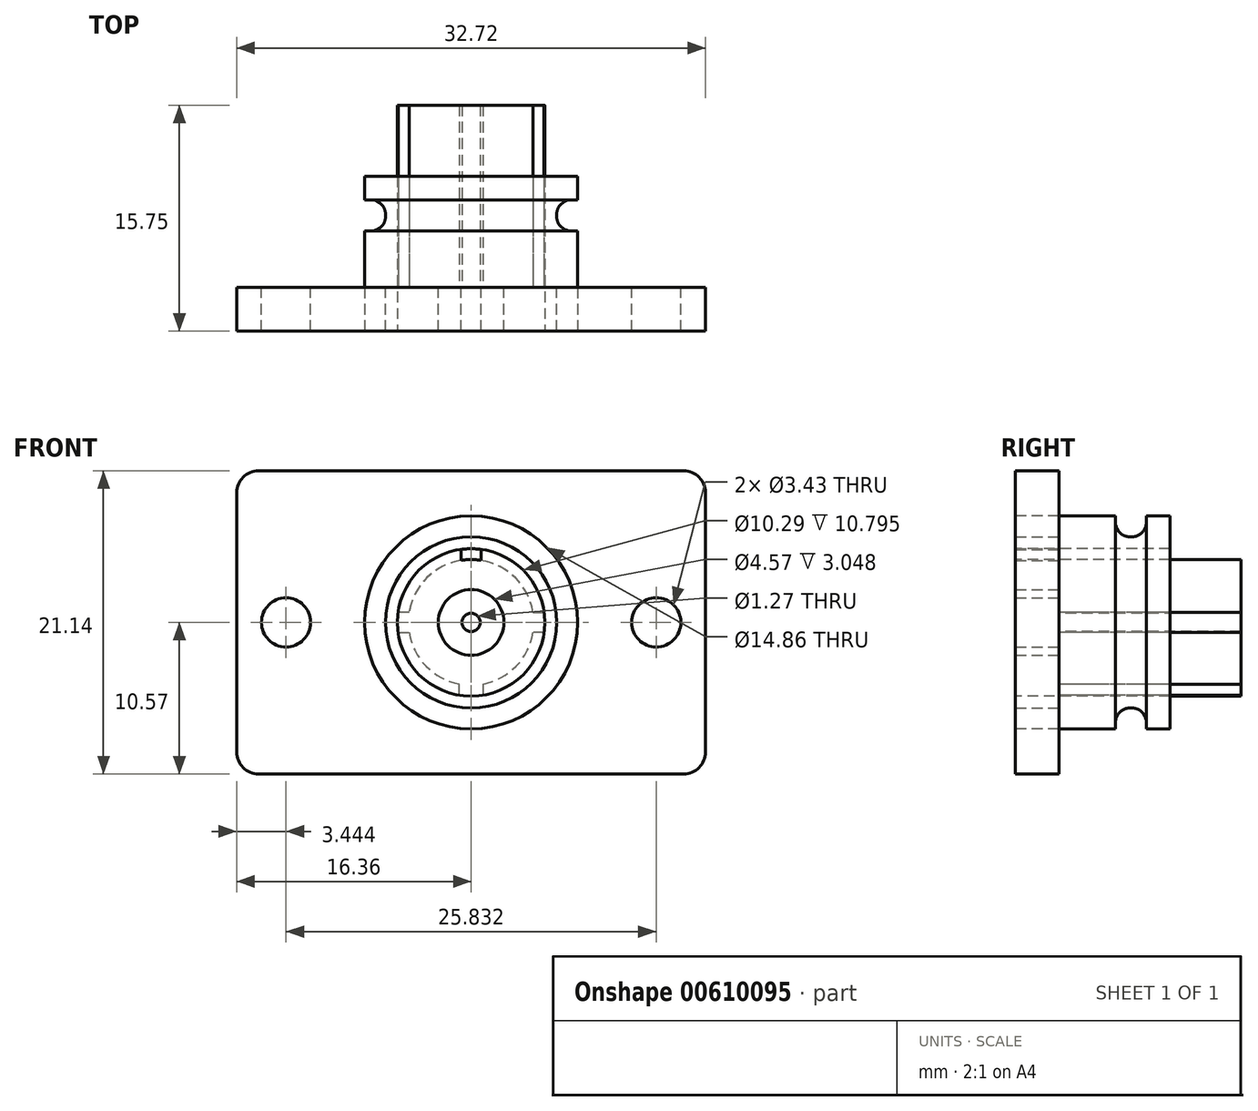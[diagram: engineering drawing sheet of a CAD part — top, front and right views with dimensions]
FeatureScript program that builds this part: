
annotation { "Feature Type Name" : "Feature", "Feature Type Description" : "" }
export const myFeature = defineFeature(function(context is Context, id is Id, definition is map)
    precondition{}
    {
        {
            var Q0;
            Q0=qCreatedBy(makeId("Front.planeOp"),FACE);
            var sketch = newSketch(context, id + "F0", { "sketchPlane" : qUnion([Q0])});
            skLineSegment(sketch, "E0.bottom", {"start": v(14.83, 10.57) * mm, "end": v(-14.83, 10.57) * mm});
            skLineSegment(sketch, "E0.top", {"start": v(14.83, -10.57) * mm, "end": v(-14.83, -10.57) * mm});
            skLineSegment(sketch, "E0.left", {"start": v(16.36, 9.04) * mm, "end": v(16.36, -9.04) * mm});
            skLineSegment(sketch, "E0.right", {"start": v(-16.36, 9.04) * mm, "end": v(-16.36, -9.04) * mm});
            skPoint(sketch, "E0.middle", {"position": v(0, 0) * mm});
            skCircle(sketch, "E1", {"center": v(12.92, 0) * mm, "radius": 1.71 * mm});
            skCircle(sketch, "E2", {"center": v(-12.92, 0) * mm, "radius": 1.71 * mm});
            skCircle(sketch, "E3", {"center": v(0, 0) * mm, "radius": 2.03 * mm});
            skCircle(sketch, "E4", {"center": v(0, 0) * mm, "radius": 2.29 * mm});
            skCircle(sketch, "E5", {"center": v(0, 0) * mm, "radius": 4.38 * mm});
            skLineSegment(sketch, "E6", {"start": v(-4.33, 0.7) * mm, "end": v(-5.09, 0.7) * mm});
            skLineSegment(sketch, "E7", {"start": v(-5.09, -0.7) * mm, "end": v(-4.33, -0.7) * mm});
            skLineSegment(sketch, "E8", {"start": v(4.33, 0.7) * mm, "end": v(5.09, 0.7) * mm});
            skLineSegment(sketch, "E9", {"start": v(5.09, -0.7) * mm, "end": v(4.33, -0.7) * mm});
            skLineSegment(sketch, "E10", {"start": v(0.7, 4.33) * mm, "end": v(0.7, 5.09) * mm});
            skLineSegment(sketch, "E11", {"start": v(-0.7, 5.09) * mm, "end": v(-0.7, 4.33) * mm});
            skArc(sketch, "E12", {"start": v(-5.09, 0.7) * mm, "mid": v(3.63, -3.63) * mm, "end": v(-0.7, 5.09) * mm});
            skLineSegment(sketch, "E13", {"start": v(-0.7, 5.09) * mm, "end": v(-0.7, 5.09) * mm});
            skLineSegment(sketch, "E14.MirrorCS", {"start": v(0.7, 5.09) * mm, "end": v(0.7, 4.33) * mm});
            skLineSegment(sketch, "E15.MirrorCS", {"start": v(-0.7, 4.33) * mm, "end": v(-0.7, 5.09) * mm});
            skArc(sketch, "E16", {"start": v(-0.7, 5.09) * mm, "mid": v(-3.63, 3.63) * mm, "end": v(-5.09, 0.7) * mm});
            skLineSegment(sketch, "E17", {"start": v(0.82, -4.3) * mm, "end": v(0.82, -5.07) * mm});
            skLineSegment(sketch, "E18", {"start": v(-0.82, -5.07) * mm, "end": v(-0.82, -4.3) * mm});
            skCircle(sketch, "E19", {"center": v(0, 0) * mm, "radius": 7.43 * mm});
            skCircle(sketch, "E20", {"center": v(0, 0) * mm, "radius": 5.97 * mm});
            skPoint(sketch, "E21.visualSharp", {"position": v(-16.36, 10.57) * mm});
            skArc(sketch, "E21.filletArc", {"start": v(-14.83, 10.57) * mm, "mid": v(-15.91, 10.12) * mm, "end": v(-16.36, 9.04) * mm});
            skPoint(sketch, "E22.visualSharp", {"position": v(-16.36, -10.57) * mm});
            skArc(sketch, "E22.filletArc", {"start": v(-16.36, -9.04) * mm, "mid": v(-15.91, -10.12) * mm, "end": v(-14.83, -10.57) * mm});
            skPoint(sketch, "E23.visualSharp", {"position": v(16.36, -10.57) * mm});
            skArc(sketch, "E23.filletArc", {"start": v(14.83, -10.57) * mm, "mid": v(15.91, -10.12) * mm, "end": v(16.36, -9.04) * mm});
            skPoint(sketch, "E24.visualSharp", {"position": v(16.36, 10.57) * mm});
            skArc(sketch, "E24.filletArc", {"start": v(16.36, 9.04) * mm, "mid": v(15.91, 10.12) * mm, "end": v(14.83, 10.57) * mm});
            skPoint(sketch, "E25.endSnap0", {"position": v(-16.36, 0) * mm});
            skCircle(sketch, "E26", {"center": v(0, 0) * mm, "radius": 0.64 * mm});
            skSolve(sketch);
        }
        {
            var Q0;
            Q0 = qSketchRegion(id + "F0", true);
            extrude(context, id + "F1", {"entities" : qUnion([Q0]), "depth" : 3.05 * mm, "offsetDistance" : 25.4 * mm});
        }
        {
            var Q0;
            {var subQ0=sQuery(id+"F0.wireOp",EDGE,"E8");Q0=makeQuery(id+"F0.imprint","IMPRINT",FACE,{"disambiguationData":[TD([[makeQuery(id+"F0.imprint","IMPRINT",EDGE,{"derivedFrom":subQ0}),-1.0]])]});}
            var Q1;
            Q1=makeQuery(id+"F0.imprint","IMPRINT",FACE,{"disambiguationData":[TD([[makeQuery(id+"F0.imprint","IMPRINT",EDGE,{"derivedFrom":sQuery(id+"F0.wireOp",EDGE,"E4")}),-1.0]])]});
            var Q2;
            {var subQ0=sQuery(id+"F0.wireOp",EDGE,"E17");Q2=makeQuery(id+"F0.imprint","IMPRINT",FACE,{"disambiguationData":[TD([[makeQuery(id+"F0.imprint","IMPRINT",EDGE,{"derivedFrom":subQ0}),-1.0]])]});}
            var Q3;
            {var subQ0=sQuery(id+"F0.wireOp",EDGE,"E6");Q3=makeQuery(id+"F0.imprint","IMPRINT",FACE,{"disambiguationData":[TD([[makeQuery(id+"F0.imprint","IMPRINT",EDGE,{"derivedFrom":subQ0}),1.0]])]});}
            var Q4;
            Q4=makeQuery(id+"F0.imprint","IMPRINT",FACE,{"disambiguationData":[TD([[makeQuery(id+"F0.imprint","IMPRINT",EDGE,{"derivedFrom":sQuery(id+"F0.wireOp",EDGE,"8aa54b31-4197-416b-9f73-8f9571a17bba2.MirrorCS")}),-1.0]])]});
            var Q5;
            {var subQ0=sQuery(id+"F0.wireOp",EDGE,"E15.MirrorCS");Q5=makeQuery(id+"F0.imprint","IMPRINT",FACE,{"disambiguationData":[TD([[makeQuery(id+"F0.imprint","IMPRINT",EDGE,{"derivedFrom":subQ0}),-1.0]])]});}
            var Q6;
            Q6=makeQuery(id+"F0.imprint","IMPRINT",FACE,{"disambiguationData":[TD([[makeQuery(id+"F0.imprint","IMPRINT",EDGE,{"derivedFrom":sQuery(id+"F0.wireOp",EDGE,"E3")}),-1.0]])]});
            extrude(context, id + "F2", {"entities" : qUnion([Q0, Q1, Q2, Q3, Q4, Q5, Q6]), "depth" : -12.7 * mm, "offsetDistance" : 25.4 * mm});
        }
        {
            var Q0;
            {var subQ0=sQuery(id+"F0.wireOp",EDGE,"ZeHlMGJi-U5nD-rJSf-8bKy-MKMc3yEPTVGU");Q0=makeQuery(id+"F0.imprint","IMPRINT",FACE,{"disambiguationData":[TD([[makeQuery(id+"F0.imprint","IMPRINT",EDGE,{"derivedFrom":subQ0}),1.0]])]});}
            var Q1;
            {var subQ0=sQuery(id+"F0.wireOp",EDGE,"E8");Q1=makeQuery(id+"F0.imprint","IMPRINT",FACE,{"disambiguationData":[TD([[makeQuery(id+"F0.imprint","IMPRINT",EDGE,{"derivedFrom":subQ0}),-1.0]])]});}
            var Q2;
            {var subQ8=sQuery(id+"F0.wireOp",EDGE,"E16");Q2=makeQuery(id+"F0.imprint","IMPRINT",FACE,{"disambiguationData":[TD([[makeQuery(id+"F0.imprint","IMPRINT",EDGE,{"derivedFrom":subQ8}),-1.0]])]});}
            var Q3;
            {var subQ0=sQuery(id+"F0.wireOp",EDGE,"E9");Q3=makeQuery(id+"F0.imprint","IMPRINT",FACE,{"disambiguationData":[TD([[makeQuery(id+"F0.imprint","IMPRINT",EDGE,{"derivedFrom":subQ0}),1.0]])]});}
            var Q4;
            Q4=makeQuery(id+"F0.imprint","IMPRINT",FACE,{"disambiguationData":[TD([[makeQuery(id+"F0.imprint","IMPRINT",EDGE,{"derivedFrom":sQuery(id+"F0.wireOp",EDGE,"E4")}),-1.0]])]});
            var Q5;
            {var subQ0=sQuery(id+"F0.wireOp",EDGE,"E8");Q5=makeQuery(id+"F0.imprint","IMPRINT",FACE,{"disambiguationData":[TD([[makeQuery(id+"F0.imprint","IMPRINT",EDGE,{"derivedFrom":subQ0}),1.0]])]});}
            var Q6;
            {var subQ0=sQuery(id+"F0.wireOp",EDGE,"E17");Q6=makeQuery(id+"F0.imprint","IMPRINT",FACE,{"disambiguationData":[TD([[makeQuery(id+"F0.imprint","IMPRINT",EDGE,{"derivedFrom":subQ0}),-1.0]])]});}
            var Q7;
            {var subQ0=sQuery(id+"F0.wireOp",EDGE,"E7");Q7=makeQuery(id+"F0.imprint","IMPRINT",FACE,{"disambiguationData":[TD([[makeQuery(id+"F0.imprint","IMPRINT",EDGE,{"derivedFrom":subQ0}),-1.0]])]});}
            var Q8;
            {var subQ0=sQuery(id+"F0.wireOp",EDGE,"E6");Q8=makeQuery(id+"F0.imprint","IMPRINT",FACE,{"disambiguationData":[TD([[makeQuery(id+"F0.imprint","IMPRINT",EDGE,{"derivedFrom":subQ0}),1.0]])]});}
            var Q9;
            {var subQ0=sQuery(id+"F0.wireOp",EDGE,"E6");Q9=makeQuery(id+"F0.imprint","IMPRINT",FACE,{"disambiguationData":[TD([[makeQuery(id+"F0.imprint","IMPRINT",EDGE,{"derivedFrom":subQ0}),-1.0]])]});}
            var Q10;
            Q10=makeQuery(id+"F0.imprint","IMPRINT",FACE,{"disambiguationData":[TD([[makeQuery(id+"F0.imprint","IMPRINT",EDGE,{"derivedFrom":sQuery(id+"F0.wireOp",EDGE,"8aa54b31-4197-416b-9f73-8f9571a17bba2.MirrorCS")}),-1.0]])]});
            var Q11;
            {var subQ0=sQuery(id+"F0.wireOp",EDGE,"8aa54b31-4197-416b-9f73-8f9571a17bba2.MirrorCS");Q11=makeQuery(id+"F0.imprint","IMPRINT",FACE,{"disambiguationData":[TD([[makeQuery(id+"F0.imprint","IMPRINT",EDGE,{"derivedFrom":subQ0}),1.0]])]});}
            var Q12;
            {var subQ0=sQuery(id+"F0.wireOp",EDGE,"5Tk1WabR-ANaY-RywQ-UzY8-5ZMrk3N4MROS");Q12=makeQuery(id+"F0.imprint","IMPRINT",FACE,{"disambiguationData":[TD([[makeQuery(id+"F0.imprint","IMPRINT",EDGE,{"derivedFrom":subQ0}),-1.0]])]});}
            var Q13;
            {var subQ0=sQuery(id+"F0.wireOp",EDGE,"8KnzkotE-2pe1-5BcI-FaJd-2mQ7kcLGwGro");Q13=makeQuery(id+"F0.imprint","IMPRINT",FACE,{"disambiguationData":[TD([[makeQuery(id+"F0.imprint","IMPRINT",EDGE,{"derivedFrom":subQ0}),1.0]])]});}
            var Q14;
            {var subQ0=sQuery(id+"F0.wireOp",EDGE,"E15.MirrorCS");Q14=makeQuery(id+"F0.imprint","IMPRINT",FACE,{"disambiguationData":[TD([[makeQuery(id+"F0.imprint","IMPRINT",EDGE,{"derivedFrom":subQ0}),-1.0]])]});}
            extrude(context, id + "F3", {"entities" : qUnion([Q0, Q1, Q2, Q3, Q4, Q5, Q6, Q7, Q8, Q9, Q10, Q11, Q12, Q13, Q14]), "depth" : 3.05 * mm, "offsetDistance" : 25.4 * mm});
        }
        {
            var Q0;
            Q0=qCreatedBy(makeId("Right.planeOp"),FACE);
            var sketch = newSketch(context, id + "F4", { "sketchPlane" : qUnion([Q0])});
            skLineSegment(sketch, "E27", {"start": v(0, 0) * mm, "end": v(19.56, 0) * mm, "construction": true});
            skLineSegment(sketch, "E28", {"start": v(-3.05, 5.14) * mm, "end": v(7.75, 5.14) * mm});
            skLineSegment(sketch, "E29", {"start": v(7.75, 5.14) * mm, "end": v(7.75, 7.43) * mm});
            skLineSegment(sketch, "E30", {"start": v(-3.05, 5.14) * mm, "end": v(-3.05, 7.43) * mm});
            skLineSegment(sketch, "E31", {"start": v(7.75, 7.43) * mm, "end": v(6.1, 7.43) * mm});
            skLineSegment(sketch, "E32", {"start": v(6.1, 7.43) * mm, "end": v(6.1, 5.97) * mm});
            skLineSegment(sketch, "E33", {"start": v(6.1, 5.97) * mm, "end": v(3.94, 5.97) * mm});
            skLineSegment(sketch, "E34", {"start": v(3.94, 5.97) * mm, "end": v(3.94, 7.43) * mm});
            skLineSegment(sketch, "E35", {"start": v(3.94, 7.43) * mm, "end": v(-3.05, 7.43) * mm});
            skLineSegment(sketch, "E36", {"start": v(-4.57, -2.29) * mm, "end": v(-10.67, -2.29) * mm});
            skPoint(sketch, "E37.visualSharp", {"position": v(-3.05, -2.29) * mm});
            skArc(sketch, "E37.filletArc", {"start": v(-3.05, -3.81) * mm, "mid": v(-3.5, -2.73) * mm, "end": v(-4.57, -2.29) * mm});
            skPoint(sketch, "E38.visualSharp", {"position": v(-3.05, 2.29) * mm});
            skLineSegment(sketch, "E39", {"start": v(-3.05, 0) * mm, "end": v(-10.67, 0) * mm});
            skLineSegment(sketch, "E40", {"start": v(-3.05, 0) * mm, "end": v(-3.05, 0.63) * mm});
            skLineSegment(sketch, "E41", {"start": v(-3.05, 0.63) * mm, "end": v(-10.67, 0.63) * mm});
            skLineSegment(sketch, "E42", {"start": v(-10.67, 0.63) * mm, "end": v(-10.67, -0.64) * mm});
            skLineSegment(sketch, "E43", {"start": v(-10.67, -0.64) * mm, "end": v(-3.05, -0.64) * mm});
            skLineSegment(sketch, "E44", {"start": v(-3.05, -0.64) * mm, "end": v(-3.05, 0) * mm});
            skLineSegment(sketch, "E45", {"start": v(-3.05, -3.81) * mm, "end": v(-3.05, -0.64) * mm});
            skLineSegment(sketch, "E46", {"start": v(-10.67, -2.29) * mm, "end": v(-10.67, -0.64) * mm});
            skLineSegment(sketch, "E47", {"start": v(-3.05, -2.29) * mm, "end": v(0, -2.29) * mm});
            skLineSegment(sketch, "E48", {"start": v(-3.05, 2.29) * mm, "end": v(0, 2.29) * mm});
            skLineSegment(sketch, "E49", {"start": v(0, 0) * mm, "end": v(-3.05, 0) * mm});
            skLineSegment(sketch, "E50", {"start": v(-3.05, 0.63) * mm, "end": v(0, 0.63) * mm});
            skLineSegment(sketch, "E51", {"start": v(-3.05, -0.64) * mm, "end": v(0, -0.64) * mm});
            skLineSegment(sketch, "E52", {"start": v(-3.05, 2.29) * mm, "end": v(-3.05, 0.63) * mm});
            skLineSegment(sketch, "E53", {"start": v(0, 2.29) * mm, "end": v(0, 0.63) * mm});
            skSolve(sketch);
        }
        {
            var Q0;
            Q0=makeQuery(id+"F4.imprint","IMPRINT",FACE,{"disambiguationData":[TD([[makeQuery(id+"F4.imprint","IMPRINT",EDGE,{"derivedFrom":sQuery(id+"F4.wireOp",EDGE,"E28")}),1.0]])]});
            var Q1;
            Q1=sQuery(id+"F4.wireOp",EDGE,"E27");
            revolve(context, id + "F5", {"entities" : qUnion([Q0]), "axis" : qUnion([Q1]), "revolveType" : RevolveType.FULL});
        }
        {
            var Q0;
            Q0=makeQuery(id+"F5.opRevolve","SWEPT_EDGE",EDGE,{"disambiguationData":[OSD([sQuery(id+"F4.wireOp",EDGE,"E32"),sQuery(id+"F4.wireOp",EDGE,"E33")])]});
            var Q1;
            Q1=makeQuery(id+"F5.opRevolve","SWEPT_EDGE",EDGE,{"disambiguationData":[OSD([sQuery(id+"F4.wireOp",EDGE,"E33"),sQuery(id+"F4.wireOp",EDGE,"E34")])]});
            fillet(context, id + "F6", {"entities" : qUnion([Q0, Q1]), "radius" : 1.02 * mm, "tangentPropagation" : true, "allowEdgeOverflow" : false});
        }
        {
            var Q0;
            Q0 = qSketchRegion(id + "F4", true);
            var Q1;
            Q1=sQuery(id+"F4.wireOp",EDGE,"E43");
            var Q2;
            Q2=sQuery(id+"F4.wireOp",EDGE,"E45");
            var Q3;
            Q3=sQuery(id+"F4.wireOp",EDGE,"E37.filletArc");
            var Q4;
            Q4=sQuery(id+"F4.wireOp",EDGE,"E36");
            var Q5;
            Q5=sQuery(id+"F4.wireOp",EDGE,"E46");
            var Q6;
            Q6=sQuery(id+"F4.wireOp",EDGE,"E39");
            revolve(context, id + "F7", {"bodyType" : ToolBodyType.SURFACE, "entities" : qUnion([Q0]), "surfaceEntities" : qUnion([Q1, Q2, Q3, Q4, Q5]), "axis" : qUnion([Q6]), "revolveType" : RevolveType.FULL});
        }
        {
            var Q0;
            Q0 = qSketchRegion(id + "F4", true);
            var Q1;
            Q1=sQuery(id+"F4.wireOp",EDGE,"E48");
            var Q2;
            Q2=sQuery(id+"F4.wireOp",EDGE,"E50");
            var Q3;
            Q3=sQuery(id+"F4.wireOp",EDGE,"E52");
            var Q4;
            Q4=sQuery(id+"F4.wireOp",EDGE,"E53");
            var Q5;
            Q5=sQuery(id+"F4.wireOp",EDGE,"E49");
            revolve(context, id + "F8", {"bodyType" : ToolBodyType.SURFACE, "entities" : qUnion([Q0]), "surfaceEntities" : qUnion([Q1, Q2, Q3, Q4]), "axis" : qUnion([Q5]), "revolveType" : RevolveType.FULL});
        }
        {
            var Q0;
            Q0=makeQuery(id+"F8.opRevolve","SWEPT_FACE",FACE,{"disambiguationData":[OSD([sQuery(id+"F4.wireOp",EDGE,"E53")])]});
            extrude(context, id + "F9", {"entities" : qUnion([Q0]), "operationType" : NewBodyOperationType.ADD, "oppositeDirection" : true, "depth" : 12.7 * mm, "offsetDistance" : 25.4 * mm});
        }
    });
